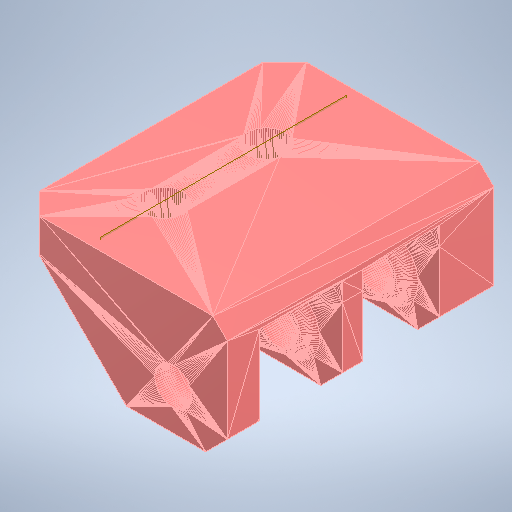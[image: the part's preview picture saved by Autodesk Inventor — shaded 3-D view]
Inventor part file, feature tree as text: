
AUTODESK INVENTOR PART (.ipt)
format: ipt  version: 2025.2 (Build 292293000, 293)  size: 259,072 bytes
history: native  units: in
note: dims shown in document units (in); Inventor stores cm internally (conversion verified against a paired STEP export)
features: other x2, plane x1
ambient origin geometry x8: Origin, YZ Plane, XZ Plane, XY Plane, X Axis, Y Axis, Z Axis, Center Point
feature tree (3):
  other  "1 X Left_Idler_Mount"
  plane  "Work Plane1"
  other  "MeshFeature1"
